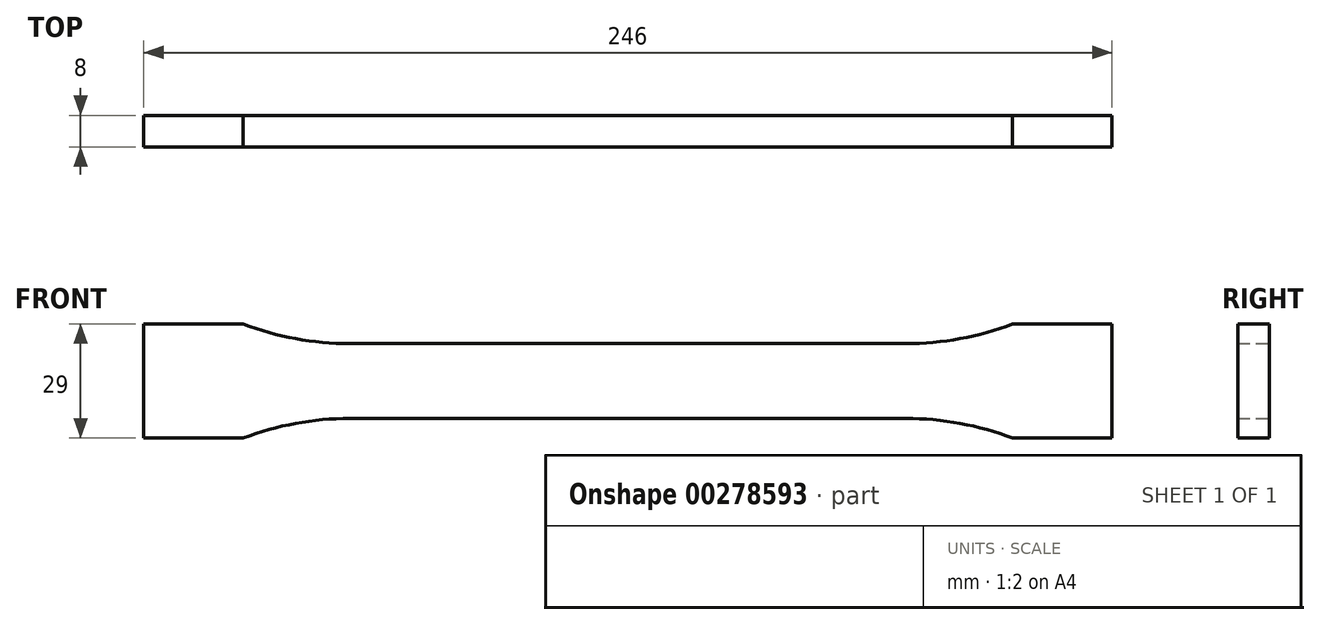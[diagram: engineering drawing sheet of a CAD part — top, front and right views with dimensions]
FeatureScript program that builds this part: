
annotation { "Feature Type Name" : "Feature", "Feature Type Description" : "" }
export const myFeature = defineFeature(function(context is Context, id is Id, definition is map)
    precondition{}
    {
        {
            var Q0;
            Q0=qCreatedBy(makeId("Front.planeOp"),FACE);
            var sketch = newSketch(context, id + "F0", { "sketchPlane" : qUnion([Q0])});
            skLineSegment(sketch, "E0", {"start": v(0, 9.5) * mm, "end": v(70.64, 9.5) * mm});
            skArc(sketch, "E1", {"start": v(70.64, 9.5) * mm, "mid": v(84.43, 10.76) * mm, "end": v(97.75, 14.5) * mm});
            skLineSegment(sketch, "E2", {"start": v(97.75, 14.5) * mm, "end": v(123, 14.5) * mm});
            skArc(sketch, "E3.MirrorCS", {"start": v(70.64, -9.5) * mm, "mid": v(84.43, -10.76) * mm, "end": v(97.75, -14.5) * mm});
            skLineSegment(sketch, "E4.MirrorCS", {"start": v(97.75, -14.5) * mm, "end": v(123, -14.5) * mm});
            skLineSegment(sketch, "E5.MirrorCS", {"start": v(0, -9.5) * mm, "end": v(70.64, -9.5) * mm});
            skArc(sketch, "E6.MirrorCS", {"start": v(-70.64, -9.5) * mm, "mid": v(-84.43, -10.76) * mm, "end": v(-97.75, -14.5) * mm});
            skLineSegment(sketch, "E7.MirrorCS", {"start": v(0, -9.5) * mm, "end": v(-70.64, -9.5) * mm});
            skArc(sketch, "E8.MirrorCS", {"start": v(-70.64, 9.5) * mm, "mid": v(-84.43, 10.76) * mm, "end": v(-97.75, 14.5) * mm});
            skLineSegment(sketch, "E9.MirrorCS", {"start": v(-97.75, -14.5) * mm, "end": v(-123, -14.5) * mm});
            skLineSegment(sketch, "E10.MirrorCS", {"start": v(-97.75, 14.5) * mm, "end": v(-123, 14.5) * mm});
            skLineSegment(sketch, "E11.MirrorCS", {"start": v(0, 9.5) * mm, "end": v(-70.64, 9.5) * mm});
            skLineSegment(sketch, "E12", {"start": v(-123, 14.5) * mm, "end": v(-123, -14.5) * mm});
            skLineSegment(sketch, "E13", {"start": v(123, 14.5) * mm, "end": v(123, -14.5) * mm});
            skSolve(sketch);
        }
        {
            var Q0;
            Q0 = qSketchRegion(id + "F0", true);
            extrude(context, id + "F1", {"entities" : qUnion([Q0]), "endBound" : BoundingType.SYMMETRIC, "depth" : 8 * mm});
        }
    });
